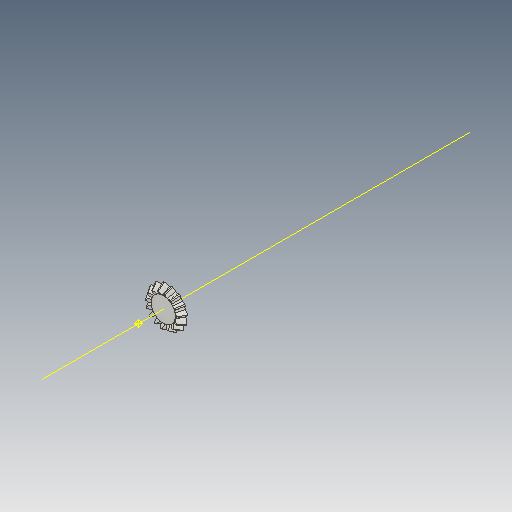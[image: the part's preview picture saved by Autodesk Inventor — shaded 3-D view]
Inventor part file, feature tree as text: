
AUTODESK INVENTOR PART (.ipt)
format: ipt  version: 2021 (Build 250183000, 183)  size: 470,016 bytes
history: native  units: mm
features: other x16, sketch x9, loft x3, pattern_circular x3
ambient origin geometry x6: Origin, XZ Plane, X Axis, Y Axis, Z Axis, Center Point
bodies: Solid1 (feature_tree)
feature tree (31):
  other  "Ponto superior"
  other  "Plano de malha 2"
  other  "Corpo dentado"
  other  "Ponto inicial"
  other  "Plano de dente"
  sketch  "Esboço inicial"  dims[d2=3.011827mm]
  other  "Extremidade"
  loft  "Loft"
  pattern_circular  "Circular Pattern"  [2 undecoded]
  sketch  "Esboço 3D direito"  dims[d3=0.6mm]
  other  "Plano final direito"
  loft  "Transição direita"
  pattern_circular  "Padrão circular direito"  [2 undecoded]
  sketch  "Esboço 3D esquerdo"  dims[d4=2.25005mm]
  other  "Plano final esquerdo"
  loft  "Transição esquerda"
  pattern_circular  "Padrão circular esquerdo"  Count=15 Angle=90.0deg
  other  "Fixar corpo"
  other  "Plano de malha"
  other  "Plano superior"
  sketch  "Esboço de corpo dentado"  dims[d5=90.0deg]
  other  "Plano final"
  sketch  "Esboço final"  dims[d7=0.593251mm]
  other  "Helical Curve Left"
  sketch  "Esboço final esquerdo"  dims[d8=0.674555mm]
  sketch  "Esboço de corpo"  dims[d9=1.289096mm]
  sketch  "Sketch6"  dims[d0=2.7mm d1=2.325808mm]
  other  "Srf1"
  other  "Helical Curve Right"
  sketch  "Esboço final direita"  dims[d11=0.6198mm d12=0.457143mm d15=0.519793mm d16=0.993341mm d17=0.0mm d18=90.0deg d19=0.0mm d20=90.0deg d21=150.0mm d22=360.0deg d26=17.944705mm d27=0.536862mm d28=2.7mm d29=-5.232783mm d30=0.457143mm d31=0.519793mm d32=0.993341mm d35=0.0mm d37=0.0mm d39=0.0mm d40=90.0deg d41=150.0mm d42=360.0deg d46=90.0deg d47=90.0deg d48=0.0mm d49=0.0mm d50=90.0deg d51=2.094395mm d52=0.0mm d53=0.0mm d54=0.0mm d56=1.014717mm d57=1.857357mm d58=1.295037mm d59=1.431227mm d60=0.997919mm d61=1.431227mm d62=0.997919mm d65=17.944705mm d66=31.5mm d67=2.7mm d68=-5.232783mm d69=0.536862mm d70=0.519793mm d71=0.993341mm d72=0.457143mm d73=0.997919mm d74=1.431227mm d75=0.0mm d77=0.0mm d79=0.0mm d80=90.0deg d81=150.0mm d82=360.0deg d84=10.0mm d85=20.0mm d86=20.0mm d87=10.0mm d88=0.0mm d89=0.0mm d90=90.0deg d91=90.0deg d92=90.0deg d93=90.0deg]
  other  "Diâmetro do flanco"
note: 4 required parameter values undecoded (feature->parameter linkage not recoverable at this tier; creation-order binding heuristic only, values carry confidence <= 0.55)
